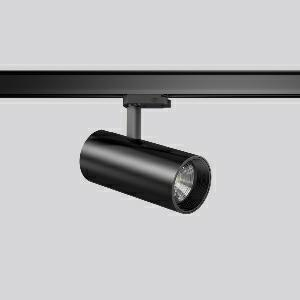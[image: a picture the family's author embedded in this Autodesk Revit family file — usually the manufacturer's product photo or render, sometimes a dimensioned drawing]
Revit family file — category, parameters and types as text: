
# Revit family: deecos_s_mini_742207_003_3_76_597b
name_source: partatom
category: Lighting Fixtures
units: mm (PartAtom-declared; Revit-internal decimal feet)

## family parameters
Cut with Voids When Loaded = No
Host = Face
Light Source = No
Part Type = Normal
Room Calculation Point = No
Round Connector Dimension = Use Diameter
Shared = No

## types (1)
- DEECOS S mini (1 x LED Modul 935, 3050 lm, 3500)
    Apparent Load = 29 VA
    Approval mark = CE
    CIE Flux Codes = 96 100 100 100 100
    Color Rendering = 92
    Color Temperature = 3500
    Default Elevation = 1800 mm
    Description = Series: DEECOS S mini
LED surface-mounted projector in modern design with no visible cooling ribs. Housing: die-cast aluminium, powder-coated. Rotation range: 356°. Swivel range: 90°. Black plastic ring and recessed LED to prevent glare from the side. Optical assembly with lens made of plastic (polycarbonate) for the best homogeneous light distribution - can be changed without tools. Best colour rendering index Ra>90. With adapter for RZB 3-circuit DALI tracks. Suitable for Track on ceiling, Wall track. High quality converter without flickering and stroboscopic effect. The following accessories can be mounted without use of tools: interchangeable lenses, decorative glasses, honeycomb louvre, clear and frosted diffusers, white interchangeable plastic ring. 
Colour: deep black, matt (RAL 9005)
Diameter: 87 mm
Height: 214 mm
Lamp: LED
Socket: without socket
Colour temperature: 3500K
Colour rendering index (CRI): 92
System power: 29 W
Rated luminous flux: 3050 lm
Luminous efficiency: 105 lm/W
Control gear: Converter, dimmable, DALI
Protection class: I
Type of protection: IP 20
    Height = 214 mm
    Lamp = 1 x LED Modul 935
    Lamp Light Flux = 3050 lm
    Lamp count = 1
    Length = 87 mm
    Lifetime = 50000 h
    Luminous efficacy = 105 lm/W
    Manufacturer = RZB
    ModVariant = No
    Model = 742207.003.3.76
    Mounting Place = Ceiling
    Mounting Type = Rail mounted
    Number of Poles = 1
    OnlyDefault = Yes
    Power Factor = 1
    Product Name = DEECOS S mini
    Product group = Track mounted projectors
    ProductGroupID = 301
    Protection Class = Protection class I
    Protection Degree = IP 20
    RLX_Detail_Level = 1
    RLX_Emergency_Light_Flux = 0 lm
    RLX_Emergency_Type = 0
    RLX_Emergency_Type_DB = No
    RlxData = <blob elided: 38997 chars, md5=339e2184>
    Socket = socket
    Standby Power = 0 W
    System Light Flux = 3050 lm
    System Power = 29 W
    Type Comments = Product without accessories
    Type Image = 741930.003.jpg
    URL = http://relux.com
    VarID = ---
    Voltage = 230 V
    Voltage Range = 220-240 V
    Weight = 0.00 kg
    Width = 0 mm  [stored 0 ft]

note: [stored X ft] marks values corroborated as IEEE doubles in the binary element streams (Revit-internal decimal feet)

## geometry (parser evidence)
native form markers: Blend x4, Sweep x12
no freeform markers — native parametric forms only
